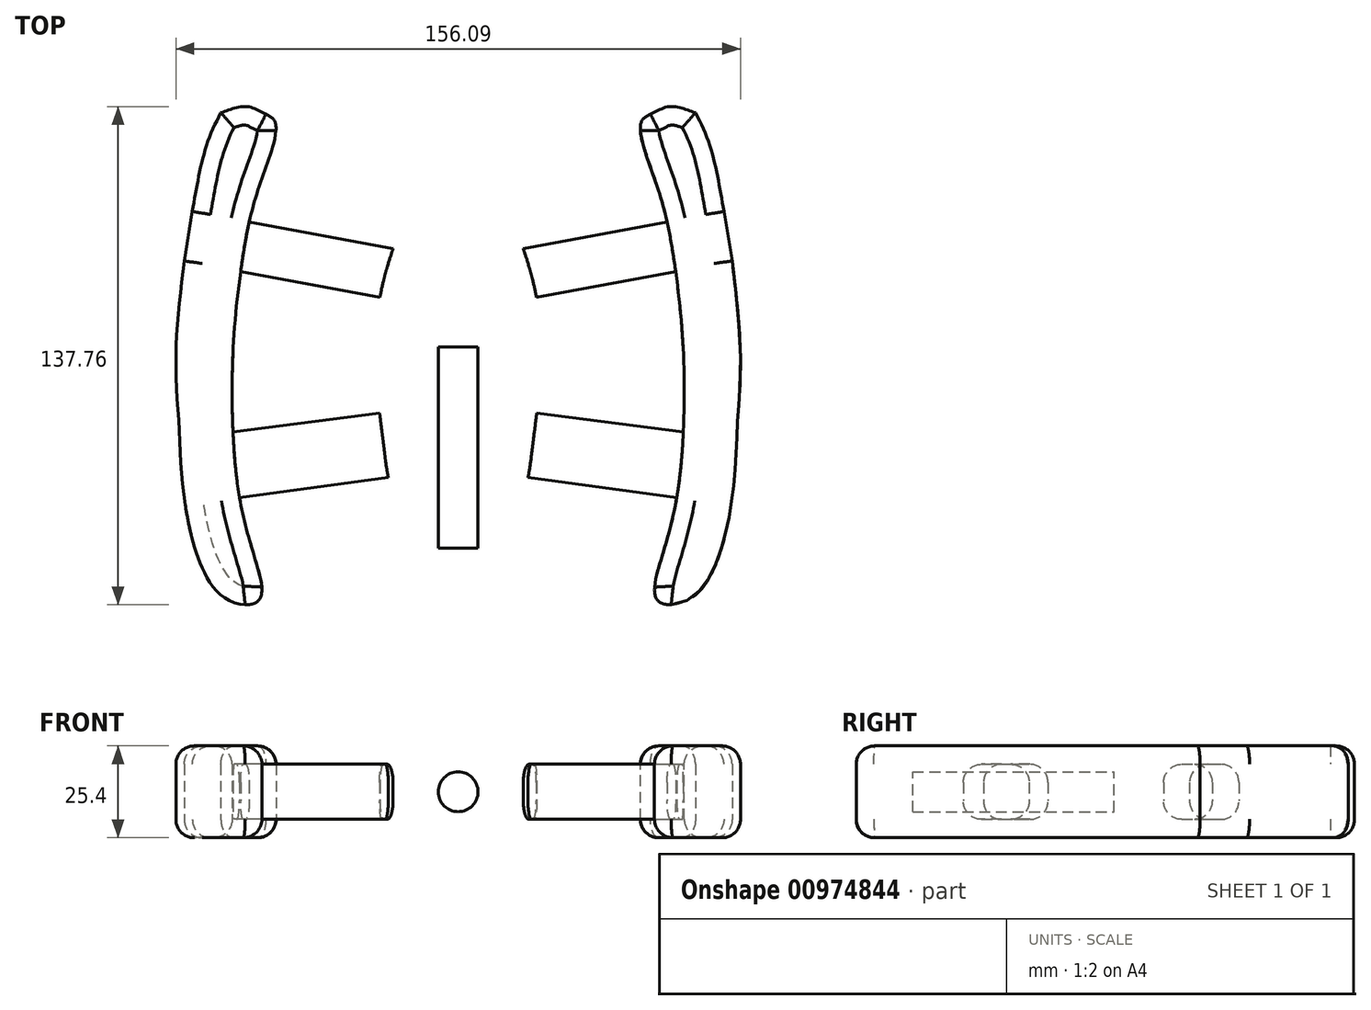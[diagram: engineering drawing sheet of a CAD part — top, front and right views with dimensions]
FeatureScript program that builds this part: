
annotation { "Feature Type Name" : "Feature", "Feature Type Description" : "" }
export const myFeature = defineFeature(function(context is Context, id is Id, definition is map)
    precondition{}
    {
        {
            var Q0;
            Q0=qCreatedBy(makeId("Top.planeOp"),FACE);
            var sketch = newSketch(context, id + "F0", { "sketchPlane" : qUnion([Q0])});
            skFitSpline(sketch, "E0", {"points": [v(0, -52.59) * mm, v(-8.2, -51.55) * mm, v(-12.84, -48.97) * mm, v(-16.45, -44.33) * mm, v(-19.3, -36.07) * mm, v(-20.58, -27.3) * mm, v(-22.13, -14.13) * mm, v(-22.65, 0) * mm, v(-21.62, 13.74) * mm, v(-18, 27.16) * mm, v(-13.1, 37.49) * mm, v(-5.87, 43.68) * mm, v(0, 44.72) * mm], "startDerivative": vector(-114.27, 6.7) * mm, "endDerivative": vector(88.38, 3.78) * mm});
            skLineSegment(sketch, "E1", {"start": v(-18, 27.16) * mm, "end": v(-57.76, 34.56) * mm});
            skLineSegment(sketch, "E2", {"start": v(-21.62, 13.74) * mm, "end": v(-60.13, 20.9) * mm});
            skPoint(sketch, "E3.orphan", {"position": v(-21.62, -13.74) * mm});
            skPoint(sketch, "E4.orphan", {"position": v(-18, -27.16) * mm});
            skLineSegment(sketch, "E5", {"start": v(-20.54, -27.64) * mm, "end": v(-20.54, -27.64) * mm});
            skLineSegment(sketch, "E6", {"start": v(-20.54, -27.64) * mm, "end": v(-20.55, -27.57) * mm});
            skLineSegment(sketch, "E7", {"start": v(-20.55, -27.57) * mm, "end": v(-20.54, -27.64) * mm});
            skLineSegment(sketch, "E8", {"start": v(-21.72, -18.22) * mm, "end": v(-62.25, -23.41) * mm});
            skLineSegment(sketch, "E9", {"start": v(-19.3, -36.07) * mm, "end": v(-60.44, -41.63) * mm});
            skFitSpline(sketch, "E10", {"points": [v(-65.6, 64.78) * mm, v(-69.62, 55.61) * mm, v(-73.5, 37.49) * mm], "startDerivative": vector(-10.05, -19.57) * mm, "endDerivative": vector(-5.92, -34.26) * mm});
            skFitSpline(sketch, "E11", {"points": [v(-73.5, 37.49) * mm, v(-75.75, 23.81) * mm], "startDerivative": vector(-2.26, -13.67) * mm, "endDerivative": vector(-2.26, -13.67) * mm});
            skPoint(sketch, "E12.11.internal.snap0", {"position": v(-45.75, 32.33) * mm});
            skFitSpline(sketch, "E12", {"points": [v(-75.75, 23.81) * mm, v(-77.78, 3.95) * mm, v(-77.91, -10.3) * mm, v(-77.12, -22.98) * mm, v(-75.75, -41.5) * mm, v(-65.6, -68.51) * mm, v(-55.2, -70.06) * mm, v(-55.97, -59.2) * mm, v(-60.44, -41.63) * mm, v(-62.46, -17.15) * mm, v(-61.69, 7.04) * mm, v(-58.23, 32.33) * mm, v(-54.01, 47.35) * mm, v(-50.56, 62.02) * mm, v(-54.01, 64.78) * mm, v(-58.4, 66.47) * mm, v(-65.6, 64.78) * mm], "startDerivative": vector(-34.3, -286.45) * mm, "endDerivative": vector(-176.49, -64.19) * mm});
            skLineSegment(sketch, "E13.trimOffspring", {"start": v(-75.44, -43.66) * mm, "end": v(-76.1, -43.75) * mm});
            skLineSegment(sketch, "E14", {"start": v(0, 62.02) * mm, "end": v(0, -70.03) * mm, "construction": true});
            skFitSpline(sketch, "E15.MirrorCS", {"points": [v(0, -52.59) * mm, v(8.2, -51.55) * mm, v(12.84, -48.97) * mm, v(16.45, -44.33) * mm, v(19.3, -36.07) * mm, v(20.58, -27.3) * mm, v(22.13, -14.13) * mm, v(22.65, 0) * mm, v(21.62, 13.74) * mm, v(18, 27.16) * mm, v(13.1, 37.49) * mm, v(5.87, 43.68) * mm, v(0, 44.72) * mm], "startDerivative": vector(114.27, 6.7) * mm, "endDerivative": vector(-88.38, 3.78) * mm});
            skLineSegment(sketch, "E16.MirrorCS", {"start": v(18, 27.16) * mm, "end": v(57.76, 34.56) * mm});
            skLineSegment(sketch, "E17.MirrorCS", {"start": v(21.62, 13.74) * mm, "end": v(60.13, 20.9) * mm});
            skLineSegment(sketch, "E18.MirrorCS", {"start": v(21.72, -18.22) * mm, "end": v(62.25, -23.41) * mm});
            skLineSegment(sketch, "E19.MirrorCS", {"start": v(19.3, -36.07) * mm, "end": v(60.44, -41.63) * mm});
            skFitSpline(sketch, "E20.MirrorCS", {"points": [v(75.75, 23.81) * mm, v(77.78, 3.95) * mm, v(77.91, -10.3) * mm, v(77.12, -22.98) * mm, v(75.75, -41.5) * mm, v(65.6, -68.51) * mm, v(55.2, -70.06) * mm, v(55.97, -59.2) * mm, v(60.44, -41.63) * mm, v(62.46, -17.15) * mm, v(61.69, 7.04) * mm, v(58.23, 32.33) * mm, v(54.01, 47.35) * mm, v(50.56, 62.02) * mm, v(54.01, 64.78) * mm, v(58.4, 66.47) * mm, v(65.6, 64.78) * mm], "startDerivative": vector(34.3, -286.45) * mm, "endDerivative": vector(176.49, -64.19) * mm});
            skFitSpline(sketch, "E21.MirrorCS", {"points": [v(65.6, 64.78) * mm, v(69.62, 55.61) * mm, v(73.5, 37.49) * mm], "startDerivative": vector(10.05, -19.57) * mm, "endDerivative": vector(5.92, -34.26) * mm});
            skFitSpline(sketch, "E22.MirrorCS", {"points": [v(73.5, 37.49) * mm, v(75.75, 23.81) * mm], "startDerivative": vector(2.26, -13.67) * mm, "endDerivative": vector(2.26, -13.67) * mm});
            skSolve(sketch);
        }
        {
            var Q0;
            {var subQ5=sQuery(id+"F0.wireOp",EDGE,"E6");var subQ7=makeQuery(id+"F0.imprint","IMPRINT",VERTEX,{"derivedFrom":subQ5});Q0=makeQuery(id+"F0.imprint","IMPRINT",FACE,{"disambiguationData":[TD([[makeQuery(id+"F0.imprint","IMPRINT",EDGE,{"disambiguationData":[TD([[subQ7,1.0]])],"derivedFrom":subQ5}),-1.0]])]});}
            var Q1;
            {var subQ4=sQuery(id+"F0.wireOp",EDGE,"E10");Q1=makeQuery(id+"F0.imprint","IMPRINT",FACE,{"disambiguationData":[TD([[makeQuery(id+"F0.imprint","IMPRINT",EDGE,{"derivedFrom":subQ4}),1.0]])]});}
            var Q2;
            {var subQ6=sQuery(id+"F0.wireOp",EDGE,"E21.MirrorCS");Q2=makeQuery(id+"F0.imprint","IMPRINT",FACE,{"disambiguationData":[TD([[makeQuery(id+"F0.imprint","IMPRINT",EDGE,{"derivedFrom":subQ6}),-1.0]])]});}
            extrude(context, id + "F1", {"entities" : qUnion([Q0, Q1, Q2]), "endBound" : BoundingType.SYMMETRIC, "depth" : 25.4 * mm, "offsetDistance" : 25.4 * mm});
        }
        {
            var Q0;
            {var subQ0=sQuery(id+"F0.wireOp",EDGE,"E1");Q0=makeQuery(id+"F0.imprint","IMPRINT",FACE,{"disambiguationData":[TD([[makeQuery(id+"F0.imprint","IMPRINT",EDGE,{"derivedFrom":subQ0}),1.0]])]});}
            var Q1;
            {var subQ5=sQuery(id+"F0.wireOp",EDGE,"E8");Q1=makeQuery(id+"F0.imprint","IMPRINT",FACE,{"disambiguationData":[TD([[makeQuery(id+"F0.imprint","IMPRINT",EDGE,{"derivedFrom":subQ5}),1.0]])]});}
            var Q2;
            {var subQ0=sQuery(id+"F0.wireOp",EDGE,"E16.MirrorCS");Q2=makeQuery(id+"F0.imprint","IMPRINT",FACE,{"disambiguationData":[TD([[makeQuery(id+"F0.imprint","IMPRINT",EDGE,{"derivedFrom":subQ0}),-1.0]])]});}
            var Q3;
            {var subQ0=sQuery(id+"F0.wireOp",EDGE,"E18.MirrorCS");Q3=makeQuery(id+"F0.imprint","IMPRINT",FACE,{"disambiguationData":[TD([[makeQuery(id+"F0.imprint","IMPRINT",EDGE,{"derivedFrom":subQ0}),-1.0]])]});}
            extrude(context, id + "F2", {"entities" : qUnion([Q0, Q1, Q2, Q3]), "endBound" : BoundingType.SYMMETRIC, "depth" : 15.24 * mm, "offsetDistance" : 25.4 * mm});
        }
        {
            var Q0;
            Q0=makeQuery(id+"F2.opExtrude","CAP_EDGE",EDGE,{"disambiguationData":[OSD([sQuery(id+"F0.wireOp",EDGE,"E2")])],"isStart":false});
            var Q1;
            Q1=makeQuery(id+"F2.opExtrude","CAP_EDGE",EDGE,{"disambiguationData":[OSD([sQuery(id+"F0.wireOp",EDGE,"E1")])],"isStart":false});
            var Q2;
            Q2=makeQuery(id+"F2.opExtrude","CAP_EDGE",EDGE,{"disambiguationData":[OSD([sQuery(id+"F0.wireOp",EDGE,"E8")])],"isStart":false});
            var Q3;
            Q3=makeQuery(id+"F2.opExtrude","CAP_EDGE",EDGE,{"disambiguationData":[OSD([sQuery(id+"F0.wireOp",EDGE,"E9")])],"isStart":false});
            var Q4;
            Q4=makeQuery(id+"F2.opExtrude","CAP_EDGE",EDGE,{"disambiguationData":[OSD([sQuery(id+"F0.wireOp",EDGE,"E19.MirrorCS")])],"isStart":false});
            var Q5;
            Q5=makeQuery(id+"F2.opExtrude","CAP_EDGE",EDGE,{"disambiguationData":[OSD([sQuery(id+"F0.wireOp",EDGE,"E18.MirrorCS")])],"isStart":false});
            var Q6;
            Q6=makeQuery(id+"F2.opExtrude","CAP_EDGE",EDGE,{"disambiguationData":[OSD([sQuery(id+"F0.wireOp",EDGE,"E17.MirrorCS")])],"isStart":false});
            var Q7;
            Q7=makeQuery(id+"F2.opExtrude","CAP_EDGE",EDGE,{"disambiguationData":[OSD([sQuery(id+"F0.wireOp",EDGE,"E16.MirrorCS")])],"isStart":false});
            var Q8;
            Q8=makeQuery(id+"F2.opExtrude","CAP_EDGE",EDGE,{"disambiguationData":[OSD([sQuery(id+"F0.wireOp",EDGE,"E9")])],"isStart":true});
            var Q9;
            Q9=makeQuery(id+"F2.opExtrude","CAP_EDGE",EDGE,{"disambiguationData":[OSD([sQuery(id+"F0.wireOp",EDGE,"E8")])],"isStart":true});
            var Q10;
            Q10=makeQuery(id+"F2.opExtrude","CAP_EDGE",EDGE,{"disambiguationData":[OSD([sQuery(id+"F0.wireOp",EDGE,"E19.MirrorCS")])],"isStart":true});
            var Q11;
            Q11=makeQuery(id+"F2.opExtrude","CAP_EDGE",EDGE,{"disambiguationData":[OSD([sQuery(id+"F0.wireOp",EDGE,"E18.MirrorCS")])],"isStart":true});
            var Q12;
            Q12=makeQuery(id+"F2.opExtrude","CAP_EDGE",EDGE,{"disambiguationData":[OSD([sQuery(id+"F0.wireOp",EDGE,"E17.MirrorCS")])],"isStart":true});
            var Q13;
            Q13=makeQuery(id+"F2.opExtrude","CAP_EDGE",EDGE,{"disambiguationData":[OSD([sQuery(id+"F0.wireOp",EDGE,"E16.MirrorCS")])],"isStart":true});
            var Q14;
            Q14=makeQuery(id+"F2.opExtrude","CAP_EDGE",EDGE,{"disambiguationData":[OSD([sQuery(id+"F0.wireOp",EDGE,"E1")])],"isStart":true});
            var Q15;
            Q15=makeQuery(id+"F2.opExtrude","CAP_EDGE",EDGE,{"disambiguationData":[OSD([sQuery(id+"F0.wireOp",EDGE,"E2")])],"isStart":true});
            fillet(context, id + "F3", {"entities" : qUnion([Q0, Q1, Q2, Q3, Q4, Q5, Q6, Q7, Q8, Q9, Q10, Q11, Q12, Q13, Q14, Q15]), "radius" : 5.08 * mm, "tangentPropagation" : true, "allowEdgeOverflow" : false});
        }
        {
            var Q0;
            Q0=makeQuery(id+"F1.opExtrude","CAP_FACE",FACE,{"disambiguationData":[OSD([sQuery(id+"F0.wireOp",EDGE,"E10"),sQuery(id+"F0.wireOp",EDGE,"E11"),sQuery(id+"F0.wireOp",EDGE,"E12")])],"isStart":false});
            var Q1;
            Q1=makeQuery(id+"F1.opExtrude","CAP_FACE",FACE,{"disambiguationData":[OSD([sQuery(id+"F0.wireOp",EDGE,"E20.MirrorCS"),sQuery(id+"F0.wireOp",EDGE,"E21.MirrorCS"),sQuery(id+"F0.wireOp",EDGE,"E22.MirrorCS")])],"isStart":false});
            var Q2;
            Q2=makeQuery(id+"F1.opExtrude","CAP_FACE",FACE,{"disambiguationData":[OSD([sQuery(id+"F0.wireOp",EDGE,"E10"),sQuery(id+"F0.wireOp",EDGE,"E11"),sQuery(id+"F0.wireOp",EDGE,"E12")])],"isStart":true});
            var Q3;
            Q3=makeQuery(id+"F1.opExtrude","CAP_FACE",FACE,{"disambiguationData":[OSD([sQuery(id+"F0.wireOp",EDGE,"E20.MirrorCS"),sQuery(id+"F0.wireOp",EDGE,"E21.MirrorCS"),sQuery(id+"F0.wireOp",EDGE,"E22.MirrorCS")])],"isStart":true});
            var Q4;
            Q4=makeQuery(id+"F1.opExtrude","CAP_FACE",FACE,{"disambiguationData":[OSD([sQuery(id+"F0.wireOp",EDGE,"E0"),sQuery(id+"F0.wireOp",EDGE,"E6"),sQuery(id+"F0.wireOp",EDGE,"E15.MirrorCS")])],"isStart":false});
            var Q5;
            Q5=makeQuery(id+"F1.opExtrude","CAP_FACE",FACE,{"disambiguationData":[OSD([sQuery(id+"F0.wireOp",EDGE,"E0"),sQuery(id+"F0.wireOp",EDGE,"E6"),sQuery(id+"F0.wireOp",EDGE,"E15.MirrorCS")])],"isStart":true});
            fillet(context, id + "F4", {"entities" : qUnion([Q0, Q1, Q2, Q3, Q4, Q5]), "radius" : 5.08 * mm, "tangentPropagation" : true, "allowEdgeOverflow" : false});
        }
        {
            var Q0;
            Q0=qCreatedBy(makeId("Front.planeOp"),FACE);
            var sketch = newSketch(context, id + "F5", { "sketchPlane" : qUnion([Q0])});
            skCircle(sketch, "E23", {"center": v(0, 0) * mm, "radius": 5.5 * mm});
            skSolve(sketch);
        }
        {
            var Q0;
            Q0 = qSketchRegion(id + "F5", true);
            extrude(context, id + "F6", {"entities" : qUnion([Q0]), "operationType" : NewBodyOperationType.ADD, "depth" : 55.63 * mm, "offsetDistance" : 25.4 * mm});
        }
    });
